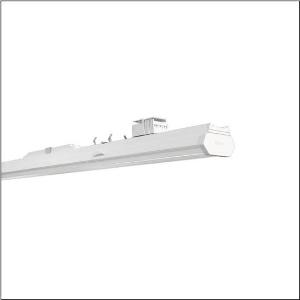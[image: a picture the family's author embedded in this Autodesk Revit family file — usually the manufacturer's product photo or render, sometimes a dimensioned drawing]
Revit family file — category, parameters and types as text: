
# Revit family: licross_11_protected_mo_51td11mn495g
name_source: partatom
category: Lighting Fixtures
units: mm (PartAtom-declared; Revit-internal decimal feet)

## family parameters
Cut with Voids When Loaded = No
Host = Face
Light Source = No
Part Type = Normal
Room Calculation Point = No
Round Connector Dimension = Use Diameter
Shared = No

## types (1)
- --- (1 x LED, 9980 lm, 55.3 W, 4000K)
    Apparent Load = 55 VA
    CIE Flux Codes = 83 94 98 100 100
    Color Rendering = 80
    Color Temperature = 4000K
    Default Elevation = 1800 mm
    Description = Licross 11 Protected MO, luminaire insert, of sheet steel, galvanised, coil coated, white, length: 1.500mm, width: 90mm, height: 101mm, LED rated luminous flux: 9.980lm, light colour: 840, SDCM (Standard Deviation of Colour Matching)MacAdam ≤ 2 SDCM (initial), control gear: ON/OFF Multilumen, with plug, 3-pole, with phase selection, mains connection: 220..240V, AC, 50/60Hz, rated input power: 55W, internal wiring halogen-free, primary light control with lens, of plastic, primary optical cover: cover, of PMMA, light emission: direct distribution, primary light characteristic: symmetric, protection rating (complete): IP54, insulation class (complete): insulation class I (protective earthing), certification: CE, ENEC, VDE, UKCA, protection symbol: D if used in an environment with non-conductive dust loads with corresponding accessories, impact resistance: IK06, permissible ambient temperature for indoor applications: -35..+40°C, corresponds to IFS (International Featured Standards) requirements for safety and quality in the food industry, reducing of maximum allowable ambient temperature of 5°C with ceiling mounting, LABS conformity tested according to VDMA 24364:2018-05, The light source and the operating device comply with the requirements of the Ecodesign Regulation (EU) 2019/2020 and are replaceable in accordance with this regulation, packaging unit: 1 piece
    Height = 92 mm
    Lamp = 1 x LED
    Lamp Light Flux = 9980 lm
    Lamp Power = 55.3 W
    Lamp count = 1
    Length = 1500 mm
    Luminous efficacy = 180 lm/W
    Manufacturer = Siteco
    ModVariant = No
    Model = 51TD11MN495G
    Mounting Place = Ceiling
    Mounting Type = Pendant
    Number of Poles = 1
    OnlyDefault = Yes
    Power Factor = 1
    Product Name = Licross 11 Protected MO
    Product group = luminaire insert | ceiling pendant
    ProductGroupID = 901
    Protection Class = Protection class I
    Protection Degree = IP 54
    RLX_Detail_Level = 1
    RLX_Emergency_Light_Flux = 0 lm
    RLX_Emergency_Type = 0
    RLX_Emergency_Type_DB = No
    RlxData = <blob elided: 22045 chars, md5=7c8543cf>
    Socket = socket
    Standby Power = 0 W
    System Light Flux = 9980 lm
    System Power = 55 W
    Type Comments = factory setting: luminous flux: 100 % | (A | C | E) | 126 mA
    Type Image = l_1256145.jpg
    URL = http://relux.com
    VarID = @adj_091961
    Voltage = 0 V
    Weight = 0.00 kg
    Width = 88 mm

## geometry (parser evidence)
native form markers: Blend x4, Sweep x9
no freeform markers — native parametric forms only
